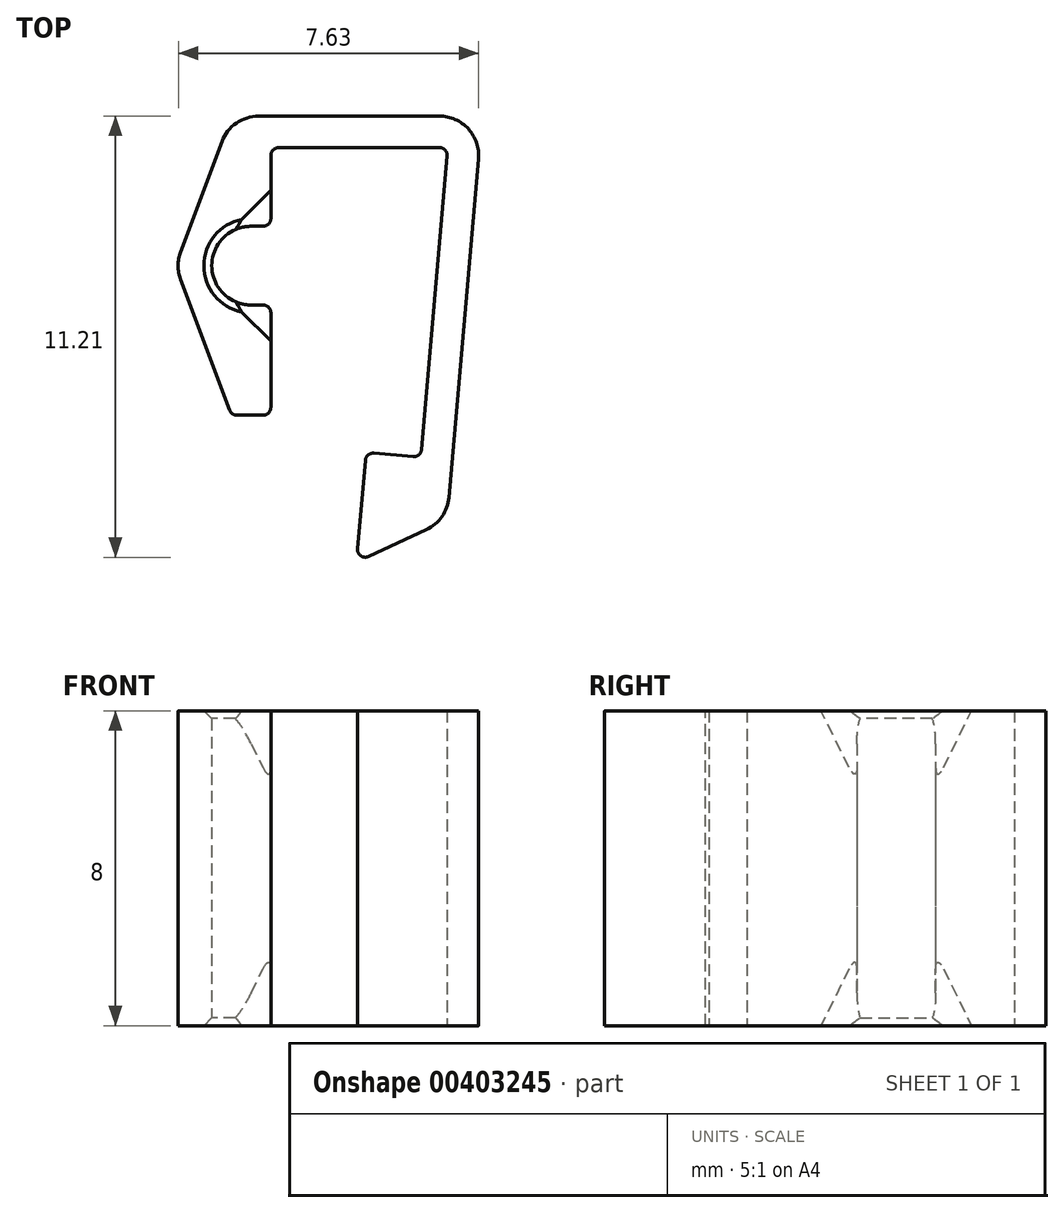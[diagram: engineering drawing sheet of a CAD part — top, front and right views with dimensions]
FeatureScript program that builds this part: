
annotation { "Feature Type Name" : "Feature", "Feature Type Description" : "" }
export const myFeature = defineFeature(function(context is Context, id is Id, definition is map)
    precondition{}
    {
        {
            var Q0;
            Q0=qCreatedBy(makeId("Top.planeOp"),FACE);
            var sketch = newSketch(context, id + "F0", { "sketchPlane" : qUnion([Q0])});
            skLineSegment(sketch, "E0", {"start": v(0, 0) * mm, "end": v(-0.69, -7.87) * mm});
            skLineSegment(sketch, "E1", {"start": v(-0.69, -7.87) * mm, "end": v(-2.08, -7.75) * mm});
            skLineSegment(sketch, "E2", {"start": v(-2.08, -7.75) * mm, "end": v(-2.33, -10.54) * mm});
            skLineSegment(sketch, "E3", {"start": v(-2.33, -10.54) * mm, "end": v(-0.02, -9.46) * mm});
            skLineSegment(sketch, "E4", {"start": v(-0.02, -9.46) * mm, "end": v(0.87, 0.8) * mm});
            skLineSegment(sketch, "E5", {"start": v(0.87, 0.8) * mm, "end": v(-5.5, 0.8) * mm});
            skLineSegment(sketch, "E6", {"start": v(-5, -4) * mm, "end": v(-4.5, -4) * mm});
            skLineSegment(sketch, "E7", {"start": v(-4.5, -4) * mm, "end": v(-4.5, -6.8) * mm});
            skLineSegment(sketch, "E8", {"start": v(-6.92, -3) * mm, "end": v(-5.5, -6.8) * mm});
            skLineSegment(sketch, "E9", {"start": v(-5.5, -6.8) * mm, "end": v(-4.5, -6.8) * mm});
            skLineSegment(sketch, "E10", {"start": v(-4.5, -2) * mm, "end": v(-5, -2) * mm});
            skLineSegment(sketch, "E11", {"start": v(0, 0) * mm, "end": v(-4.5, 0) * mm});
            skLineSegment(sketch, "E12", {"start": v(-4.5, 0) * mm, "end": v(-4.5, -2) * mm});
            skArc(sketch, "E13", {"start": v(-5, -2) * mm, "mid": v(-6, -3) * mm, "end": v(-5, -4) * mm});
            skLineSegment(sketch, "E14", {"start": v(-6.92, -3) * mm, "end": v(-5.5, 0.8) * mm});
            skLineSegment(sketch, "E15", {"start": v(-5.5, -6.8) * mm, "end": v(-5.5, 0.8) * mm, "construction": true});
            skLineSegment(sketch, "E16", {"start": v(-5, -3) * mm, "end": v(-5.94, -2.65) * mm, "construction": true});
            skLineSegment(sketch, "E17", {"start": v(-5.94, -2.65) * mm, "end": v(-6.69, -2.37) * mm, "construction": true});
            skLineSegment(sketch, "E18", {"start": v(0, 0) * mm, "end": v(0, 0.8) * mm, "construction": true});
            skLineSegment(sketch, "E19", {"start": v(0.8, -0.07) * mm, "end": v(0, 0) * mm, "construction": true});
            skSolve(sketch);
        }
        {
            var Q0;
            Q0=qSketchRegion(id+"F0",true);
            extrude(context, id + "F1", {"entities" : qUnion([Q0]), "depth" : 4 * mm});
        }
        {
            var Q0;
            Q0=makeQuery(id+"F1.opExtrude","CAP_FACE",FACE,{"disambiguationData":[OSD([sQuery(id+"F0.wireOp",EDGE,"E0"),sQuery(id+"F0.wireOp",EDGE,"E1"),sQuery(id+"F0.wireOp",EDGE,"E2"),sQuery(id+"F0.wireOp",EDGE,"E3"),sQuery(id+"F0.wireOp",EDGE,"E4"),sQuery(id+"F0.wireOp",EDGE,"E5"),sQuery(id+"F0.wireOp",EDGE,"3qQk4eZ2-qFBK-7vCE-47k8-9gwiF50xY8QG"),sQuery(id+"F0.wireOp",EDGE,"FwfflrWr-MbD4-lGZ7-AJjG-6BkzjliF19me"),sQuery(id+"F0.wireOp",EDGE,"E6"),sQuery(id+"F0.wireOp",EDGE,"E7"),sQuery(id+"F0.wireOp",EDGE,"dEJFUDGW-VdPt-nXIw-TINV-OlQtnsbTHH9Y"),sQuery(id+"F0.wireOp",EDGE,"E8"),sQuery(id+"F0.wireOp",EDGE,"E9")])],"isStart":false});
            var sketch = newSketch(context, id + "F2", { "sketchPlane" : qUnion([Q0])});
            skLineSegment(sketch, "E20", {"start": v(-5.7, -3.7) * mm, "end": v(-4.5, -4.91) * mm});
            skLineSegment(sketch, "E21", {"start": v(-4.5, -4.91) * mm, "end": v(-4.5, -4) * mm});
            skLineSegment(sketch, "E22", {"start": v(-4.5, -4) * mm, "end": v(-5.7, -3.7) * mm});
            skLineSegment(sketch, "E23", {"start": v(-5.7, -2.3) * mm, "end": v(-4.5, -1.09) * mm});
            skLineSegment(sketch, "E24", {"start": v(-4.5, -1.09) * mm, "end": v(-4.5, -2) * mm});
            skLineSegment(sketch, "E25", {"start": v(-4.5, -2) * mm, "end": v(-5.7, -2.3) * mm});
            skSolve(sketch);
        }
        {
            var Q0;
            Q0=qSketchRegion(id+"F2",true);
            extrude(context, id + "F3", {"entities" : qUnion([Q0]), "operationType" : NewBodyOperationType.REMOVE, "oppositeDirection" : true, "depth" : 2 * mm});
        }
        {
            var Q0;
            Q0=makeQuery(id+"F3.boolean.opBoolean","COPY",EDGE,{"derivedFrom":makeQuery(id+"F3.opExtrude","CAP_EDGE",EDGE,{"disambiguationData":[OSD([sQuery(id+"F2.wireOp",EDGE,"E20")])],"isStart":false})});
            chamfer(context, id + "F4", {"entities" : qUnion([Q0]), "chamferType" : ChamferType.TWO_OFFSETS, "width1" : .7 * mm, "oppositeDirection" : false, "width2" : 2 * mm, "tangentPropagation" : true});
        }
        {
            var Q0;
            Q0=makeQuery(id+"F3.boolean.opBoolean","COPY",EDGE,{"derivedFrom":makeQuery(id+"F3.opExtrude","CAP_EDGE",EDGE,{"disambiguationData":[OSD([sQuery(id+"F2.wireOp",EDGE,"E23")])],"isStart":false})});
            chamfer(context, id + "F5", {"entities" : qUnion([Q0]), "chamferType" : ChamferType.TWO_OFFSETS, "width1" : 2 * mm, "oppositeDirection" : false, "width2" : .7 * mm, "tangentPropagation" : true});
        }
        {
            var Q0;
            Q0=makeQuery(id+"F1.opExtrude","SWEPT_EDGE",EDGE,{"disambiguationData":[OSD([sQuery(id+"F0.wireOp",EDGE,"E0"),sQuery(id+"F0.wireOp",EDGE,"3qQk4eZ2-qFBK-7vCE-47k8-9gwiF50xY8QG")])]});
            var Q1;
            Q1=makeQuery(id+"F1.opExtrude","SWEPT_EDGE",EDGE,{"disambiguationData":[OSD([sQuery(id+"F0.wireOp",EDGE,"E0"),sQuery(id+"F0.wireOp",EDGE,"E1")])]});
            var Q2;
            Q2=makeQuery(id+"F1.opExtrude","SWEPT_EDGE",EDGE,{"disambiguationData":[OSD([sQuery(id+"F0.wireOp",EDGE,"E1"),sQuery(id+"F0.wireOp",EDGE,"E2")])]});
            var Q3;
            Q3=makeQuery(id+"F1.opExtrude","SWEPT_EDGE",EDGE,{"disambiguationData":[OSD([sQuery(id+"F0.wireOp",EDGE,"E2"),sQuery(id+"F0.wireOp",EDGE,"E3")])]});
            var Q4;
            Q4=makeQuery(id+"F1.opExtrude","SWEPT_EDGE",EDGE,{"disambiguationData":[OSD([sQuery(id+"F0.wireOp",EDGE,"E7"),sQuery(id+"F0.wireOp",EDGE,"E9")])]});
            var Q5;
            Q5=makeQuery(id+"F1.opExtrude","SWEPT_EDGE",EDGE,{"disambiguationData":[OSD([sQuery(id+"F0.wireOp",EDGE,"E6"),sQuery(id+"F0.wireOp",EDGE,"E7")])]});
            var Q6;
            Q6=makeQuery(id+"F1.opExtrude","SWEPT_EDGE",EDGE,{"disambiguationData":[OSD([sQuery(id+"F0.wireOp",EDGE,"E10"),sQuery(id+"F0.wireOp",EDGE,"E12")])]});
            var Q7;
            Q7=makeQuery(id+"F1.opExtrude","SWEPT_EDGE",EDGE,{"disambiguationData":[OSD([sQuery(id+"F0.wireOp",EDGE,"E8"),sQuery(id+"F0.wireOp",EDGE,"E9")])]});
            var Q8;
            Q8=makeQuery(id+"F1.opExtrude","SWEPT_EDGE",EDGE,{"disambiguationData":[OSD([sQuery(id+"F0.wireOp",EDGE,"E11"),sQuery(id+"F0.wireOp",EDGE,"E12")])]});
            fillet(context, id + "F6", {"entities" : qUnion([Q0, Q1, Q2, Q3, Q4, Q5, Q6, Q7, Q8]), "radius" : .2 * mm, "tangentPropagation" : true, "allowEdgeOverflow" : false});
        }
        {
            var Q0;
            Q0=makeQuery(id+"F1.opExtrude","SWEPT_EDGE",EDGE,{"disambiguationData":[OSD([sQuery(id+"F0.wireOp",EDGE,"E4"),sQuery(id+"F0.wireOp",EDGE,"E5")])]});
            var Q1;
            Q1=makeQuery(id+"F1.opExtrude","SWEPT_EDGE",EDGE,{"disambiguationData":[OSD([sQuery(id+"F0.wireOp",EDGE,"E3"),sQuery(id+"F0.wireOp",EDGE,"E4")])]});
            var Q2;
            Q2=makeQuery(id+"F1.opExtrude","SWEPT_EDGE",EDGE,{"disambiguationData":[OSD([sQuery(id+"F0.wireOp",EDGE,"E8"),sQuery(id+"F0.wireOp",EDGE,"E9")])]});
            var Q3;
            Q3=makeQuery(id+"F1.opExtrude","SWEPT_EDGE",EDGE,{"disambiguationData":[OSD([sQuery(id+"F0.wireOp",EDGE,"E8"),sQuery(id+"F0.wireOp",EDGE,"E14")])]});
            var Q4;
            Q4=makeQuery(id+"F1.opExtrude","SWEPT_EDGE",EDGE,{"disambiguationData":[OSD([sQuery(id+"F0.wireOp",EDGE,"E5"),sQuery(id+"F0.wireOp",EDGE,"E14")])]});
            fillet(context, id + "F7", {"entities" : qUnion([Q0, Q1, Q2, Q3, Q4]), "radius" : 1 * mm, "tangentPropagation" : true, "allowEdgeOverflow" : false});
        }
        {
            var Q0;
            Q0=makeQuery(id+"F1.opExtrude","SWEPT_BODY",BODY,{"disambiguationData":[OSD([sQuery(id+"F0.wireOp",EDGE,"E0"),sQuery(id+"F0.wireOp",EDGE,"E1"),sQuery(id+"F0.wireOp",EDGE,"E2"),sQuery(id+"F0.wireOp",EDGE,"E3"),sQuery(id+"F0.wireOp",EDGE,"E4"),sQuery(id+"F0.wireOp",EDGE,"E5"),sQuery(id+"F0.wireOp",EDGE,"3qQk4eZ2-qFBK-7vCE-47k8-9gwiF50xY8QG"),sQuery(id+"F0.wireOp",EDGE,"FwfflrWr-MbD4-lGZ7-AJjG-6BkzjliF19me"),sQuery(id+"F0.wireOp",EDGE,"E6"),sQuery(id+"F0.wireOp",EDGE,"E7"),sQuery(id+"F0.wireOp",EDGE,"dEJFUDGW-VdPt-nXIw-TINV-OlQtnsbTHH9Y"),sQuery(id+"F0.wireOp",EDGE,"E8"),sQuery(id+"F0.wireOp",EDGE,"E9")])]});
            var Q1;
            Q1=makeQuery(id+"F1.opExtrude","CAP_FACE",FACE,{"disambiguationData":[OSD([sQuery(id+"F0.wireOp",EDGE,"E0"),sQuery(id+"F0.wireOp",EDGE,"E1"),sQuery(id+"F0.wireOp",EDGE,"E2"),sQuery(id+"F0.wireOp",EDGE,"E3"),sQuery(id+"F0.wireOp",EDGE,"E4"),sQuery(id+"F0.wireOp",EDGE,"E5"),sQuery(id+"F0.wireOp",EDGE,"3qQk4eZ2-qFBK-7vCE-47k8-9gwiF50xY8QG"),sQuery(id+"F0.wireOp",EDGE,"FwfflrWr-MbD4-lGZ7-AJjG-6BkzjliF19me"),sQuery(id+"F0.wireOp",EDGE,"E6"),sQuery(id+"F0.wireOp",EDGE,"E7"),sQuery(id+"F0.wireOp",EDGE,"dEJFUDGW-VdPt-nXIw-TINV-OlQtnsbTHH9Y"),sQuery(id+"F0.wireOp",EDGE,"E8"),sQuery(id+"F0.wireOp",EDGE,"E9")])],"isStart":true});
            mirror(context, id + "F8", {"operationType" : NewBodyOperationType.ADD, "entities" : qUnion([Q0]), "mirrorPlane" : qUnion([Q1])});
        }
        {
            var Q0;
            Q0=makeQuery(id+"F1.opExtrude","CAP_EDGE",EDGE,{"disambiguationData":[OSD([sQuery(id+"F0.wireOp",EDGE,"E13")])],"isStart":false});
            var Q1;
            Q1=makeQuery(id+"F8.opPattern","COPY",EDGE,{"derivedFrom":makeQuery(id+"F1.opExtrude","CAP_EDGE",EDGE,{"disambiguationData":[OSD([sQuery(id+"F0.wireOp",EDGE,"E13")])],"isStart":false}),"instanceName":"1"});
            chamfer(context, id + "F9", {"entities" : qUnion([Q0, Q1]), "chamferType" : ChamferType.OFFSET_ANGLE, "width" : .2 * mm, "oppositeDirection" : false, "angle" : 45 * degree, "tangentPropagation" : true});
        }
    });
